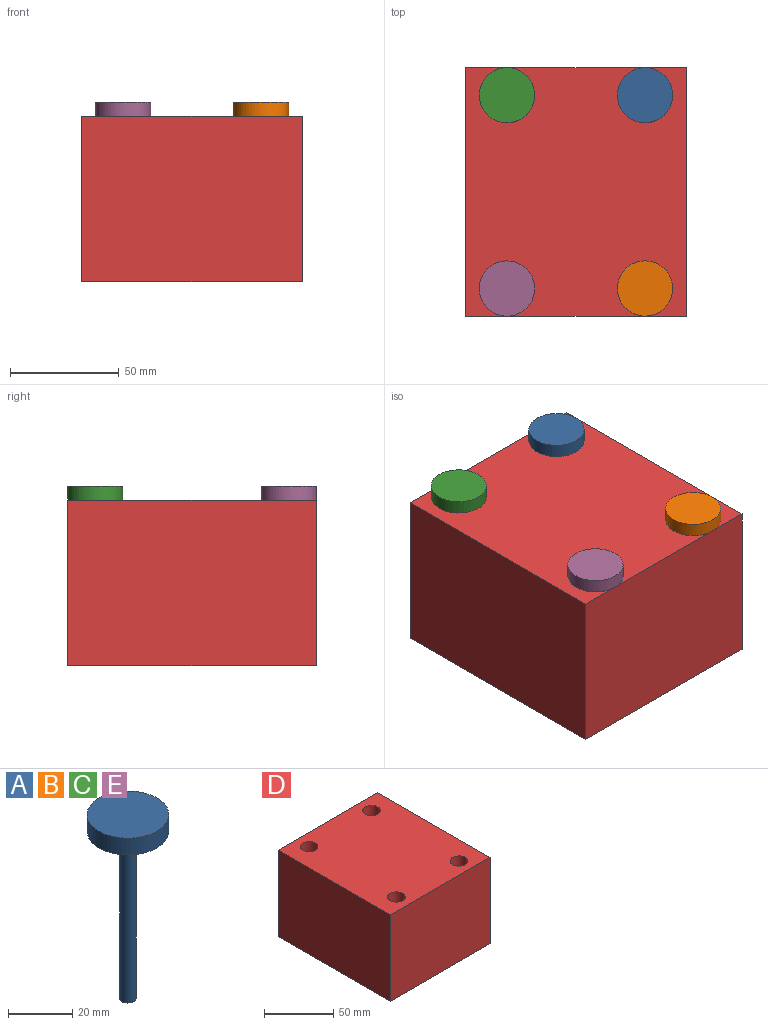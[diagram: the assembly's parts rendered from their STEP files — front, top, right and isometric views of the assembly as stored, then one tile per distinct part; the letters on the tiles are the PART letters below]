
ASSEMBLY  parts=5 mates=2
PART A: 5 faces, bbox 25.4x25.4x69.9 mm
  f0: plane 25.4x25.4mm, normal (0,0,1), area 506.7mm2, adj f4
  f1: plane 5.08x5.08mm, normal (0,0,-1), area 20.3mm2, adj f2
  f2: cylinder r=2.54mm len=63.5mm, axis (0,0,-1), area 1013.4mm2, adj f1,f3
  f3: plane 25.4x25.4mm, normal (0,0,-1), area 486.4mm2, adj f2,f4
  f4: cylinder r=12.7mm len=25.4mm, axis (0,0,-1), area 506.7mm2, adj f0,f3
PART B: same geometry as A
PART C: same geometry as A
PART D: 10 faces, bbox 101.6x114.3x76.2 mm
  f0: plane 101.6x76.2mm, normal (0,-1,0), area 7741.9mm2, adj f1,f7,f8,f9
  f1: plane 114.3x76.2mm, normal (1,0,0), area 8709.7mm2, adj f0,f2,f8,f9
  f2: plane 101.6x76.2mm, normal (0,1,0), area 7741.9mm2, adj f1,f7,f8,f9
  f3: cylinder r=6.35mm len=76.2mm, axis (0,0,-1), area 3040.2mm2, adj f8,f9
  f4: cylinder r=6.35mm len=76.2mm, axis (0,0,-1), area 3040.2mm2, adj f8,f9
  f5: cylinder r=6.35mm len=76.2mm, axis (0,0,-1), area 3040.2mm2, adj f8,f9
  f6: cylinder r=6.35mm len=76.2mm, axis (0,0,-1), area 3040.2mm2, adj f8,f9
  f7: plane 114.3x76.2mm, normal (-1,0,0), area 8709.7mm2, adj f0,f2,f8,f9
  f8: plane 114.3x101.6mm, normal (0,0,1), area 11106.2mm2, adj f0,f1,f2,f3,f4,f5,f6,f7
  f9: plane 114.3x101.6mm, normal (0,0,-1), area 11106.2mm2, adj f0,f1,f2,f3,f4,f5,f6,f7
PART E: same geometry as A
PLACE A t=(63.5,88.9,0)mm
PLACE B rot(axis=(0,0,-1),41.7deg) t=(85.02,-32.34,-0.04)mm
PLACE C t=(0,88.9,0)mm
PLACE D at identity fixed
PLACE E at identity
MATE fastened A.f2 <-> D.f3  axis (0,0,-1) through (31.75,44.45,76.2)mm
MATE cylindrical B.f2 <-> D.f6  axis (0,0,-1) through (31.75,-44.45,76.16)mm
